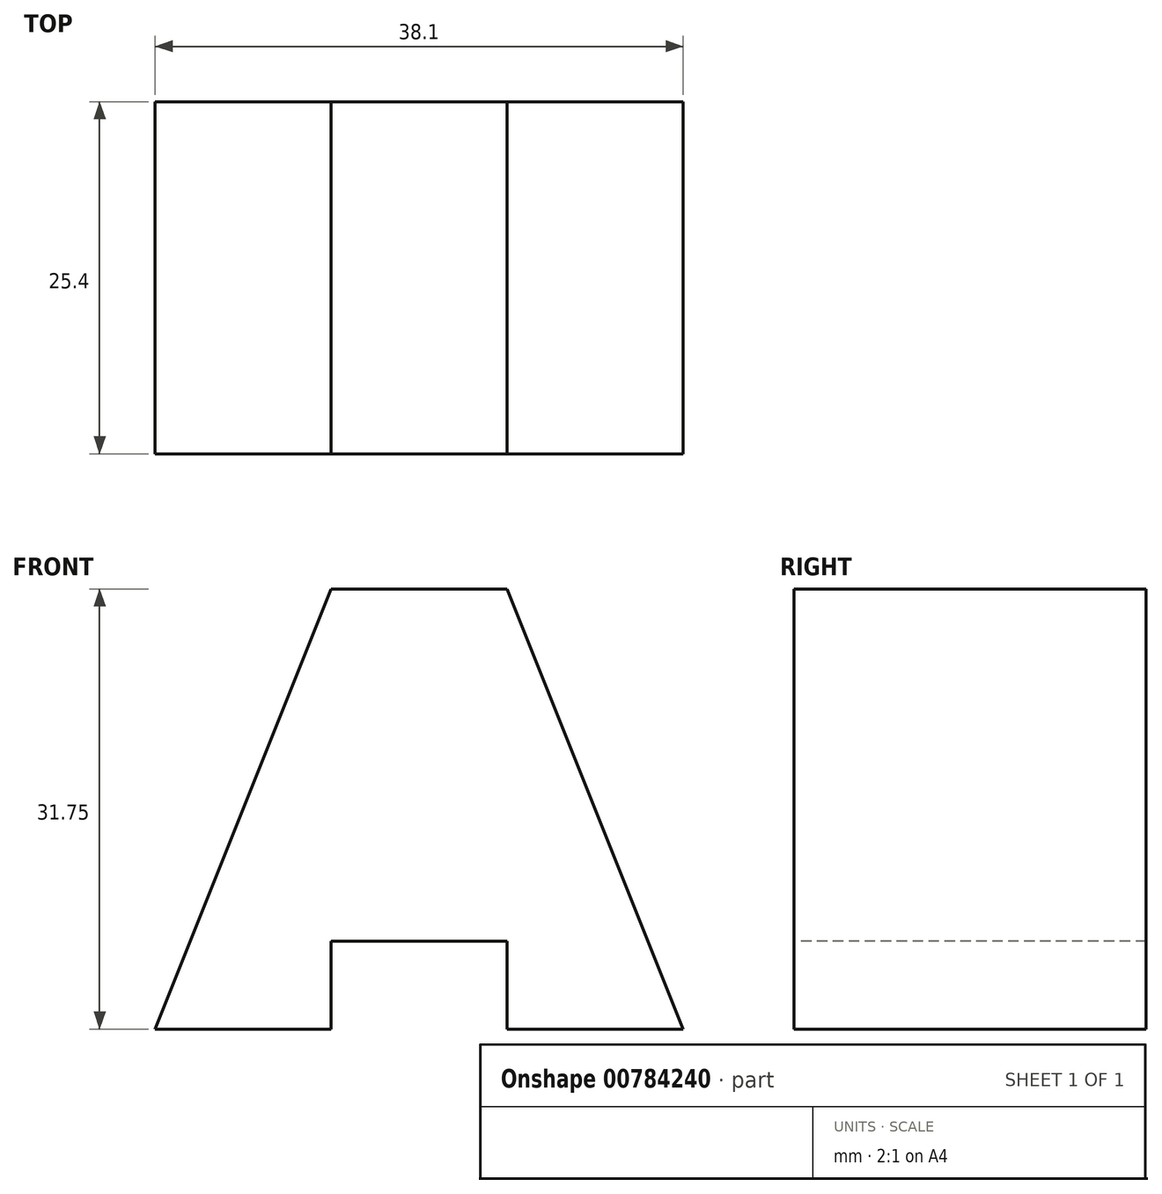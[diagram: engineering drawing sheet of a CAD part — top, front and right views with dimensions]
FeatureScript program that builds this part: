
annotation { "Feature Type Name" : "Feature", "Feature Type Description" : "" }
export const myFeature = defineFeature(function(context is Context, id is Id, definition is map)
    precondition{}
    {
        {
            var Q0;
            Q0=qCreatedBy(makeId("Front.planeOp"),FACE);
            var sketch = newSketch(context, id + "F0", { "sketchPlane" : qUnion([Q0])});
            skLineSegment(sketch, "E0", {"start": v(0, 0) * mm, "end": v(38.1, 0) * mm});
            skLineSegment(sketch, "E1", {"start": v(38.1, 0) * mm, "end": v(38.1, 31.75) * mm});
            skLineSegment(sketch, "E2", {"start": v(38.1, 31.75) * mm, "end": v(0, 31.75) * mm});
            skLineSegment(sketch, "E3", {"start": v(0, 31.75) * mm, "end": v(0, 0) * mm});
            skSolve(sketch);
        }
        {
            var Q0;
            Q0=makeQuery(id+"F0.imprint","IMPRINT",FACE,{"disambiguationData":[TD([[makeQuery(id+"F0.imprint","IMPRINT",EDGE,{"derivedFrom":sQuery(id+"F0.wireOp",EDGE,"E0")}),1.0]])]});
            extrude(context, id + "F1", {"entities" : qUnion([Q0]), "depth" : 25.4 * mm, "offsetDistance" : 25.4 * mm});
        }
        {
            var Q0;
            Q0=makeQuery(id+"F1.opExtrude","CAP_FACE",FACE,{"disambiguationData":[OSD([sQuery(id+"F0.wireOp",EDGE,"E0"),sQuery(id+"F0.wireOp",EDGE,"E1"),sQuery(id+"F0.wireOp",EDGE,"E2"),sQuery(id+"F0.wireOp",EDGE,"E3")])],"isStart":false});
            var sketch = newSketch(context, id + "F2", { "sketchPlane" : qUnion([Q0])});
            skLineSegment(sketch, "E4", {"start": v(0, 0) * mm, "end": v(12.7, 0) * mm});
            skLineSegment(sketch, "E5", {"start": v(12.7, 0) * mm, "end": v(12.7, 6.35) * mm});
            skLineSegment(sketch, "E6", {"start": v(12.7, 6.35) * mm, "end": v(25.4, 6.35) * mm});
            skLineSegment(sketch, "E7", {"start": v(25.4, 6.35) * mm, "end": v(25.4, 0) * mm});
            skLineSegment(sketch, "E8", {"start": v(25.4, 0) * mm, "end": v(38.1, 0) * mm});
            skSolve(sketch);
        }
        {
            var Q0;
            {var subQ0=sQuery(id+"F2.wireOp",EDGE,"E5");Q0=makeQuery(id+"F2.imprint","IMPRINT",FACE,{"disambiguationData":[TD([[makeQuery(id+"F2.imprint","IMPRINT",EDGE,{"derivedFrom":subQ0}),-1.0]])]});}
            extrude(context, id + "F3", {"entities" : qUnion([Q0]), "operationType" : NewBodyOperationType.REMOVE, "oppositeDirection" : true, "depth" : 25.4 * mm, "offsetDistance" : 25.4 * mm});
        }
        {
            var Q0;
            Q0=makeQuery(id+"F1.opExtrude","CAP_FACE",FACE,{"disambiguationData":[OSD([sQuery(id+"F0.wireOp",EDGE,"E0"),sQuery(id+"F0.wireOp",EDGE,"E1"),sQuery(id+"F0.wireOp",EDGE,"E2"),sQuery(id+"F0.wireOp",EDGE,"E3")])],"isStart":false});
            var sketch = newSketch(context, id + "F4", { "sketchPlane" : qUnion([Q0])});
            skLineSegment(sketch, "E9", {"start": v(38.1, 31.75) * mm, "end": v(25.4, 31.75) * mm});
            skLineSegment(sketch, "E10", {"start": v(25.4, 31.75) * mm, "end": v(12.7, 31.75) * mm});
            skLineSegment(sketch, "E11", {"start": v(12.7, 31.75) * mm, "end": v(0, 31.75) * mm});
            skLineSegment(sketch, "E12", {"start": v(0, 0) * mm, "end": v(12.7, 31.75) * mm});
            skLineSegment(sketch, "E13", {"start": v(38.1, 0) * mm, "end": v(25.4, 31.75) * mm});
            skSolve(sketch);
        }
        {
            var Q0;
            Q0=makeQuery(id+"F4.imprint","IMPRINT",FACE,{"disambiguationData":[TD([[makeQuery(id+"F4.imprint","IMPRINT",EDGE,{"derivedFrom":sQuery(id+"F4.wireOp",EDGE,"E9")}),1.0]])]});
            extrude(context, id + "F5", {"entities" : qUnion([Q0]), "operationType" : NewBodyOperationType.REMOVE, "oppositeDirection" : true, "depth" : 25.4 * mm, "offsetDistance" : 25.4 * mm});
        }
        {
            var Q0;
            Q0=makeQuery(id+"F4.imprint","IMPRINT",FACE,{"disambiguationData":[TD([[makeQuery(id+"F4.imprint","IMPRINT",EDGE,{"derivedFrom":sQuery(id+"F4.wireOp",EDGE,"E11")}),1.0]])]});
            extrude(context, id + "F6", {"entities" : qUnion([Q0]), "operationType" : NewBodyOperationType.REMOVE, "oppositeDirection" : true, "depth" : 25.4 * mm, "offsetDistance" : 25.4 * mm});
        }
    });
